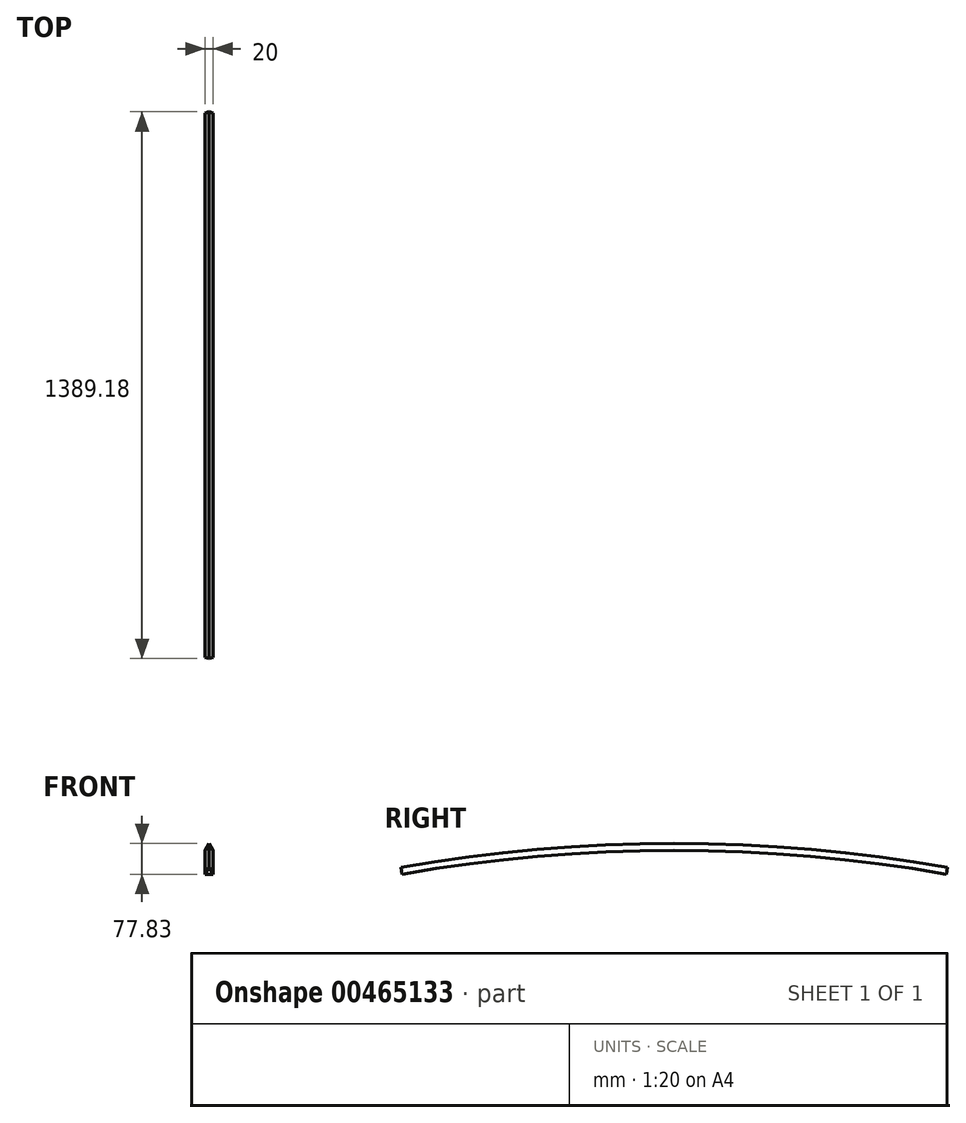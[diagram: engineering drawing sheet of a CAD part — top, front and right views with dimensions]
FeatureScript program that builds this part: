
annotation { "Feature Type Name" : "Feature", "Feature Type Description" : "" }
export const myFeature = defineFeature(function(context is Context, id is Id, definition is map)
    precondition{}
    {
        {
            var Q0;
            Q0=qCreatedBy(makeId("Front.planeOp"),FACE);
            var sketch = newSketch(context, id + "F0", { "sketchPlane" : qUnion([Q0])});
            skLineSegment(sketch, "E0", {"start": v(-40.32, 50) * mm, "end": v(-30.32, 67.32) * mm});
            skLineSegment(sketch, "E1", {"start": v(-30.32, 67.32) * mm, "end": v(-20.32, 50) * mm});
            skLineSegment(sketch, "E2", {"start": v(-20.32, 50) * mm, "end": v(-40.32, 50) * mm});
            skLineSegment(sketch, "E3", {"start": v(-42.12, -3932.68) * mm, "end": v(-14.02, -3932.68) * mm});
            skSolve(sketch);
        }
        {
            var Q0;
            Q0=makeQuery(id+"F0.imprint","IMPRINT",FACE,{"disambiguationData":[TD([[makeQuery(id+"F0.imprint","IMPRINT",EDGE,{"derivedFrom":sQuery(id+"F0.wireOp",EDGE,"E0")}),-1.0]])]});
            var Q1;
            Q1=sQuery(id+"F0.wireOp",EDGE,"E3");
            revolve(context, id + "F1", {"entities" : qUnion([Q0]), "axis" : qUnion([Q1]), "revolveType" : RevolveType.SYMMETRIC, "angle" : 20 * degree});
        }
    });
